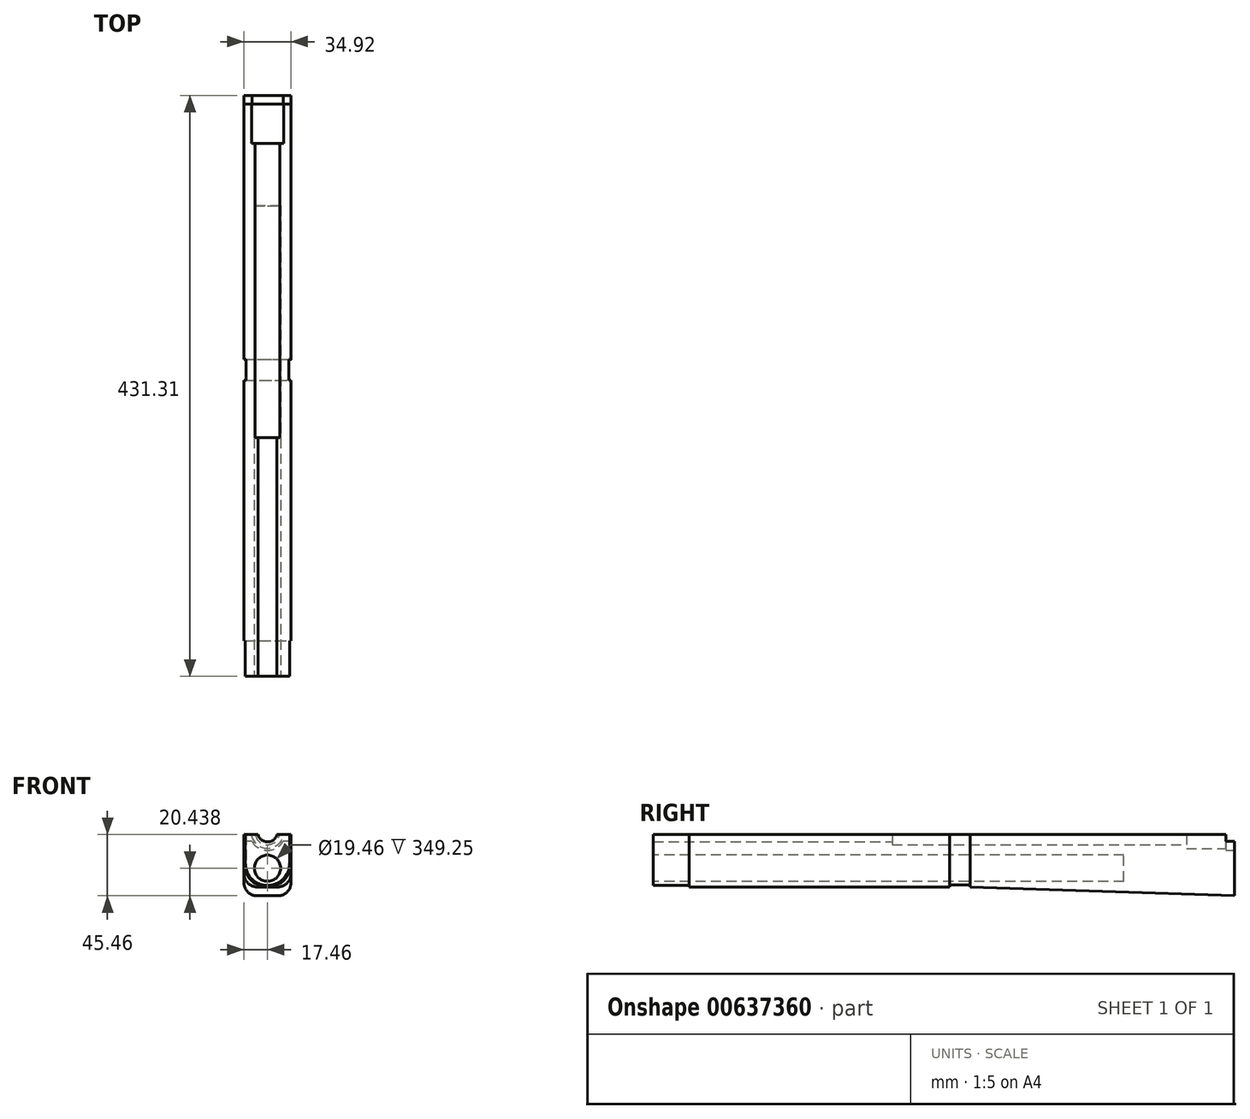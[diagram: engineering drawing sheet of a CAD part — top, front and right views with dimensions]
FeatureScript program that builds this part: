
annotation { "Feature Type Name" : "Feature", "Feature Type Description" : "" }
export const myFeature = defineFeature(function(context is Context, id is Id, definition is map)
    precondition{}
    {
        {
            var Q0;
            Q0=qCreatedBy(makeId("Front.planeOp"),FACE);
            var sketch = newSketch(context, id + "F0", { "sketchPlane" : qUnion([Q0])});
            skLineSegment(sketch, "E0", {"start": v(-17.45, -47.24) * mm, "end": v(17.45, -47.24) * mm});
            skLineSegment(sketch, "E1", {"start": v(-16.13, -1.78) * mm, "end": v(-16.13, -47.24) * mm});
            skLineSegment(sketch, "E2", {"start": v(16.13, -47.24) * mm, "end": v(16.13, -1.78) * mm});
            skLineSegment(sketch, "E3", {"start": v(-17.45, -1.78) * mm, "end": v(-17.45, -47.24) * mm});
            skLineSegment(sketch, "E4", {"start": v(17.45, -1.78) * mm, "end": v(12.57, -1.78) * mm});
            skLineSegment(sketch, "E5.trimOffspring", {"start": v(-12.57, -1.78) * mm, "end": v(-17.45, -1.78) * mm});
            skArc(sketch, "E6.converted", {"start": v(-12.57, -1.78) * mm, "mid": v(0, -12.7) * mm, "end": v(12.57, -1.78) * mm});
            skLineSegment(sketch, "E7", {"start": v(17.45, -6.83) * mm, "end": v(11.6, -6.83) * mm});
            skLineSegment(sketch, "E8", {"start": v(17.45, -1.78) * mm, "end": v(17.45, -47.24) * mm});
            skLineSegment(sketch, "E9.trimOffspring", {"start": v(-11.6, -6.83) * mm, "end": v(-17.45, -6.83) * mm});
            skArc(sketch, "E10.0", {"start": v(-13.34, -1.78) * mm, "mid": v(0, -13.46) * mm, "end": v(13.34, -1.78) * mm});
            skSolve(sketch);
        }
        {
            var Q0;
            {var subQ2=sQuery(id+"F0.wireOp",EDGE,"E2");Q0=makeQuery(id+"F0.imprint","IMPRINT",FACE,{"disambiguationData":[TD([[makeQuery(id+"F0.imprint","IMPRINT",EDGE,{"derivedFrom":subQ2}),-1.0]])]});}
            var Q1;
            {var subQ2=sQuery(id+"F0.wireOp",EDGE,"E1");Q1=makeQuery(id+"F0.imprint","IMPRINT",FACE,{"disambiguationData":[TD([[makeQuery(id+"F0.imprint","IMPRINT",EDGE,{"derivedFrom":subQ2}),-1.0]])]});}
            var Q2;
            {var subQ4=sQuery(id+"F0.wireOp",EDGE,"E1");Q2=makeQuery(id+"F0.imprint","IMPRINT",FACE,{"disambiguationData":[TD([[makeQuery(id+"F0.imprint","IMPRINT",EDGE,{"derivedFrom":subQ4}),1.0]])]});}
            var Q3;
            {var subQ0=sQuery(id+"F0.wireOp",EDGE,"E4");var subQ1=sQuery(id+"F0.wireOp",EDGE,"E2");var subQ2=makeQuery(id+"F0.imprint","INTERSECT",VERTEX,{"derivedFrom":[subQ1,subQ0]});Q3=makeQuery(id+"F0.imprint","IMPRINT",FACE,{"disambiguationData":[TD([[makeQuery(id+"F0.imprint","IMPRINT",EDGE,{"disambiguationData":[TD([[subQ2,1.0]])],"derivedFrom":subQ1}),1.0]])]});}
            var Q4;
            {var subQ0=sQuery(id+"F0.wireOp",EDGE,"E4");var subQ1=sQuery(id+"F0.wireOp",EDGE,"E2");var subQ2=makeQuery(id+"F0.imprint","INTERSECT",VERTEX,{"derivedFrom":[subQ1,subQ0]});Q4=makeQuery(id+"F0.imprint","IMPRINT",FACE,{"disambiguationData":[TD([[makeQuery(id+"F0.imprint","IMPRINT",EDGE,{"disambiguationData":[TD([[subQ2,1.0]])],"derivedFrom":subQ1}),-1.0]])]});}
            var Q5;
            {var subQ0=sQuery(id+"F0.wireOp",EDGE,"E5.trimOffspring");var subQ1=sQuery(id+"F0.wireOp",EDGE,"E1");var subQ2=makeQuery(id+"F0.imprint","INTERSECT",VERTEX,{"derivedFrom":[subQ1,subQ0]});Q5=makeQuery(id+"F0.imprint","IMPRINT",FACE,{"disambiguationData":[TD([[makeQuery(id+"F0.imprint","IMPRINT",EDGE,{"disambiguationData":[TD([[subQ2,-1.0]])],"derivedFrom":subQ1}),-1.0]])]});}
            var Q6;
            {var subQ5=sQuery(id+"F0.wireOp",EDGE,"E0");var subQ7=sQuery(id+"F0.wireOp",EDGE,"E1");var subQ8=makeQuery(id+"F0.imprint","INTERSECT",VERTEX,{"derivedFrom":[subQ5,subQ7]});Q6=makeQuery(id+"F0.imprint","IMPRINT",FACE,{"disambiguationData":[TD([[makeQuery(id+"F0.imprint","IMPRINT",EDGE,{"disambiguationData":[TD([[subQ8,-1.0]])],"derivedFrom":subQ5}),1.0]])]});}
            extrude(context, id + "F1", {"entities" : qUnion([Q0, Q1, Q2, Q3, Q4, Q5, Q6]), "depth" : 6.35 * mm, "offsetDistance" : 25.4 * mm});
        }
        {
            var Q0;
            Q0=makeQuery(id+"F1.opExtrude","CAP_FACE",FACE,{"disambiguationData":[OSD([sQuery(id+"F0.wireOp",EDGE,"E0"),sQuery(id+"F0.wireOp",EDGE,"8edb2757-4879-4a96-b7e5-693a79a6b6a4"),sQuery(id+"F0.wireOp",EDGE,"b94c221b-9bd1-4d43-af97-e907ac8222b8"),sQuery(id+"F0.wireOp",EDGE,"b538d115-4aab-44f9-98d3-6b26c575ee44"),sQuery(id+"F0.wireOp",EDGE,"78d40427-cc9b-45da-965b-9590cd821f86"),sQuery(id+"F0.wireOp",EDGE,"c01ce0f5-0f3a-4153-bfe7-1fc23657275d")])],"isStart":false});
            var sketch = newSketch(context, id + "F2", { "sketchPlane" : qUnion([Q0])});
            skLineSegment(sketch, "E11", {"start": v(-17.45, -47.24) * mm, "end": v(-17.45, -47.24) * mm});
            skArc(sketch, "E12", {"start": v(-11.93, -1.78) * mm, "mid": v(0, -12.07) * mm, "end": v(11.93, -1.78) * mm});
            skLineSegment(sketch, "E13", {"start": v(-16.13, -1.78) * mm, "end": v(-16.13, -47.24) * mm});
            skLineSegment(sketch, "E14", {"start": v(16.13, -1.78) * mm, "end": v(16.13, -47.24) * mm});
            skLineSegment(sketch, "E15", {"start": v(11.93, -1.78) * mm, "end": v(17.45, -1.78) * mm});
            skLineSegment(sketch, "E16", {"start": v(-11.93, -1.78) * mm, "end": v(-17.45, -1.78) * mm});
            skLineSegment(sketch, "E17", {"start": v(-17.45, -1.78) * mm, "end": v(-17.45, -47.24) * mm});
            skSolve(sketch);
        }
        {
            var Q0;
            {var subQ2=sQuery(id+"F2.wireOp",EDGE,"E13");Q0=makeQuery(id+"F2.imprint","IMPRINT",FACE,{"disambiguationData":[TD([[makeQuery(id+"F2.imprint","IMPRINT",EDGE,{"derivedFrom":subQ2}),1.0]])]});}
            var Q1;
            {var subQ0=sQuery(id+"F2.wireOp",EDGE,"E12");Q1=makeQuery(id+"F2.imprint","IMPRINT",FACE,{"disambiguationData":[TD([[makeQuery(id+"F2.imprint","IMPRINT",EDGE,{"derivedFrom":subQ0}),-1.0]])]});}
            var Q2;
            {var subQ0=sQuery(id+"F2.wireOp",EDGE,"E13");Q2=makeQuery(id+"F2.imprint","IMPRINT",FACE,{"disambiguationData":[TD([[makeQuery(id+"F2.imprint","IMPRINT",EDGE,{"derivedFrom":subQ0}),-1.0]])]});}
            var Q3;
            {var subQ0=sQuery(id+"F2.wireOp",EDGE,"E14");Q3=makeQuery(id+"F2.imprint","IMPRINT",FACE,{"disambiguationData":[TD([[makeQuery(id+"F2.imprint","IMPRINT",EDGE,{"derivedFrom":subQ0}),1.0]])]});}
            extrude(context, id + "F3", {"entities" : qUnion([Q0, Q1, Q2, Q3]), "operationType" : NewBodyOperationType.ADD, "depth" : 29.2 * mm, "offsetDistance" : 25.4 * mm});
        }
        {
            var Q0;
            Q0=makeQuery(id+"F3.opExtrude","CAP_FACE",FACE,{"disambiguationData":[OSD([sQuery(id+"F2.wireOp",EDGE,"E12"),sQuery(id+"F2.wireOp",EDGE,"E13"),sQuery(id+"F2.wireOp",EDGE,"E14"),sQuery(id+"F2.wireOp",EDGE,"f77e2a34-3a45-4c61-b7b2-087de49498f3"),sQuery(id+"F2.wireOp",EDGE,"be3fd59c-918e-4d32-9c2f-12a798890d1d"),sQuery(id+"F2.wireOp",EDGE,"E11")])],"isStart":false});
            var sketch = newSketch(context, id + "F4", { "sketchPlane" : qUnion([Q0])});
            skArc(sketch, "E18", {"start": v(-9.12, -1.78) * mm, "mid": v(0, -9.3) * mm, "end": v(9.12, -1.78) * mm});
            skLineSegment(sketch, "E19", {"start": v(-16.13, -1.78) * mm, "end": v(-16.13, -47.24) * mm});
            skLineSegment(sketch, "E20", {"start": v(16.13, -1.78) * mm, "end": v(16.13, -47.24) * mm});
            skLineSegment(sketch, "E21", {"start": v(17.45, -1.78) * mm, "end": v(9.12, -1.78) * mm});
            skLineSegment(sketch, "E22", {"start": v(-17.45, -1.78) * mm, "end": v(-9.12, -1.78) * mm});
            skLineSegment(sketch, "E23", {"start": v(-17.45, -47.24) * mm, "end": v(17.45, -47.24) * mm});
            skLineSegment(sketch, "E24", {"start": v(17.45, -47.24) * mm, "end": v(17.45, -1.78) * mm});
            skLineSegment(sketch, "E25", {"start": v(-17.45, -1.78) * mm, "end": v(-17.45, -47.24) * mm});
            skSolve(sketch);
        }
        {
            var Q0;
            Q0=qSketchRegion(id+"F4",true);
            extrude(context, id + "F5", {"entities" : qUnion([Q0]), "operationType" : NewBodyOperationType.ADD, "depth" : 160.5 * mm, "offsetDistance" : 25.4 * mm});
        }
        {
            var Q0;
            Q0=makeQuery(id+"F5.opExtrude","CAP_EDGE",EDGE,{"disambiguationData":[OSD([sQuery(id+"F4.wireOp",EDGE,"E23")])],"isStart":false});
            chamfer(context, id + "F6", {"entities" : qUnion([Q0]), "chamferType" : ChamferType.TWO_OFFSETS, "width1" : 6.6 * mm, "oppositeDirection" : false, "width2" : 196.06 * mm, "tangentPropagation" : true});
        }
        {
            var Q0;
            Q0=makeQuery(id+"F6.opChamfer","BLEND_EDGE",EDGE,{"blendedFrom":[makeQuery(id+"F5.opExtrude","CAP_EDGE",EDGE,{"disambiguationData":[OSD([sQuery(id+"F4.wireOp",EDGE,"E23")])],"isStart":false}),makeQuery(id+"F5.boolean.opBoolean","MERGE",FACE,{"derivedFrom":[makeQuery(id+"F3.boolean.opBoolean","MERGE",FACE,{"derivedFrom":[makeQuery(id+"F1.opExtrude","SWEPT_FACE",FACE,{"disambiguationData":[OSD([sQuery(id+"F0.wireOp",EDGE,"E3")])]}),makeQuery(id+"F3.opExtrude","SWEPT_FACE",FACE,{"disambiguationData":[OSD([sQuery(id+"F2.wireOp",EDGE,"E17")])]})]}),makeQuery(id+"F5.opExtrude","SWEPT_FACE",FACE,{"disambiguationData":[OSD([sQuery(id+"F4.wireOp",EDGE,"E25")])]})]})],"blendedInto":[makeQuery(id+"F5.boolean.opBoolean","MERGE",FACE,{"derivedFrom":[makeQuery(id+"F3.boolean.opBoolean","MERGE",FACE,{"derivedFrom":[makeQuery(id+"F1.opExtrude","SWEPT_FACE",FACE,{"disambiguationData":[OSD([sQuery(id+"F0.wireOp",EDGE,"E3")])]}),makeQuery(id+"F3.opExtrude","SWEPT_FACE",FACE,{"disambiguationData":[OSD([sQuery(id+"F2.wireOp",EDGE,"E17")])]})]}),makeQuery(id+"F5.opExtrude","SWEPT_FACE",FACE,{"disambiguationData":[OSD([sQuery(id+"F4.wireOp",EDGE,"E25")])]})]})]});
            var Q1;
            Q1=makeQuery(id+"F6.opChamfer","BLEND_EDGE",EDGE,{"blendedFrom":[makeQuery(id+"F5.opExtrude","CAP_EDGE",EDGE,{"disambiguationData":[OSD([sQuery(id+"F4.wireOp",EDGE,"E23")])],"isStart":false}),makeQuery(id+"F5.boolean.opBoolean","MERGE",FACE,{"derivedFrom":[makeQuery(id+"F3.boolean.opBoolean","MERGE",FACE,{"derivedFrom":[makeQuery(id+"F1.opExtrude","SWEPT_FACE",FACE,{"disambiguationData":[OSD([sQuery(id+"F0.wireOp",EDGE,"2a34f45b-83aa-449b-ac8a-cdb24f63008b")])]}),makeQuery(id+"F3.opExtrude","SWEPT_FACE",FACE,{"disambiguationData":[OSD([sQuery(id+"F2.wireOp",EDGE,"fa13c2eb-5be7-4b32-a947-3f863f632ee6")])]})]}),makeQuery(id+"F5.opExtrude","SWEPT_FACE",FACE,{"disambiguationData":[OSD([sQuery(id+"F4.wireOp",EDGE,"E24")])]})]})],"blendedInto":[makeQuery(id+"F5.boolean.opBoolean","MERGE",FACE,{"derivedFrom":[makeQuery(id+"F3.boolean.opBoolean","MERGE",FACE,{"derivedFrom":[makeQuery(id+"F1.opExtrude","SWEPT_FACE",FACE,{"disambiguationData":[OSD([sQuery(id+"F0.wireOp",EDGE,"2a34f45b-83aa-449b-ac8a-cdb24f63008b")])]}),makeQuery(id+"F3.opExtrude","SWEPT_FACE",FACE,{"disambiguationData":[OSD([sQuery(id+"F2.wireOp",EDGE,"fa13c2eb-5be7-4b32-a947-3f863f632ee6")])]})]}),makeQuery(id+"F5.opExtrude","SWEPT_FACE",FACE,{"disambiguationData":[OSD([sQuery(id+"F4.wireOp",EDGE,"E24")])]})]})]});
            fillet(context, id + "F7", {"entities" : qUnion([Q0, Q1]), "radius" : 9.65 * mm, "tangentPropagation" : true, "allowEdgeOverflow" : false});
        }
        {
            var Q0;
            Q0=makeQuery(id+"F5.opExtrude","CAP_FACE",FACE,{"disambiguationData":[OSD([sQuery(id+"F4.wireOp",EDGE,"E18"),sQuery(id+"F4.wireOp",EDGE,"E21"),sQuery(id+"F4.wireOp",EDGE,"E22"),sQuery(id+"F4.wireOp",EDGE,"E23"),sQuery(id+"F4.wireOp",EDGE,"E24"),sQuery(id+"F4.wireOp",EDGE,"E25")])],"isStart":false});
            var sketch = newSketch(context, id + "F8", { "sketchPlane" : qUnion([Q0])});
            skLineSegment(sketch, "E26.0", {"start": v(-15.92, -1.78) * mm, "end": v(-15.93, -23.19) * mm});
            skLineSegment(sketch, "E27.0", {"start": v(15.92, -1.78) * mm, "end": v(15.93, -23.19) * mm});
            skArc(sketch, "E28", {"start": v(-15.93, -23.19) * mm, "mid": v(0, -39.12) * mm, "end": v(15.93, -23.19) * mm});
            skLineSegment(sketch, "E29", {"start": v(-15.92, -1.78) * mm, "end": v(-9.12, -1.78) * mm});
            skLineSegment(sketch, "E30", {"start": v(15.92, -1.78) * mm, "end": v(9.12, -1.78) * mm});
            skArc(sketch, "E31", {"start": v(-9.12, -1.78) * mm, "mid": v(0, -9.3) * mm, "end": v(9.12, -1.78) * mm});
            skSolve(sketch);
        }
        {
            var Q0;
            Q0=makeQuery(id+"F8.imprint","IMPRINT",FACE,{"disambiguationData":[TD([[makeQuery(id+"F8.imprint","IMPRINT",EDGE,{"derivedFrom":sQuery(id+"F8.wireOp",EDGE,"E26.0")}),1.0]])]});
            extrude(context, id + "F9", {"entities" : qUnion([Q0]), "operationType" : NewBodyOperationType.ADD, "depth" : 15.42 * mm, "offsetDistance" : 25.4 * mm});
        }
        {
            var Q0;
            Q0=makeQuery(id+"F9.opExtrude","CAP_FACE",FACE,{"disambiguationData":[OSD([sQuery(id+"F8.wireOp",EDGE,"E26.0"),sQuery(id+"F8.wireOp",EDGE,"E27.0"),sQuery(id+"F8.wireOp",EDGE,"E28"),sQuery(id+"F8.wireOp",EDGE,"E29"),sQuery(id+"F8.wireOp",EDGE,"E30"),sQuery(id+"F8.wireOp",EDGE,"E31")])],"isStart":false});
            var sketch = newSketch(context, id + "F10", { "sketchPlane" : qUnion([Q0])});
            skLineSegment(sketch, "E32", {"start": v(9.12, -1.78) * mm, "end": v(17.46, -1.78) * mm});
            skArc(sketch, "E33", {"start": v(-9.12, -1.78) * mm, "mid": v(0, -9.3) * mm, "end": v(9.12, -1.78) * mm});
            skLineSegment(sketch, "E34.MirrorCS", {"start": v(-9.12, -1.78) * mm, "end": v(-17.46, -1.78) * mm});
            skLineSegment(sketch, "E35.MirrorCS", {"start": v(17.46, -1.78) * mm, "end": v(17.46, -23.18) * mm});
            skLineSegment(sketch, "E36.MirrorCS", {"start": v(-17.46, -1.78) * mm, "end": v(-17.46, -23.18) * mm});
            skArc(sketch, "E37", {"start": v(-17.46, -23.18) * mm, "mid": v(0, -40.64) * mm, "end": v(17.46, -23.18) * mm});
            skSolve(sketch);
        }
        {
            var Q0;
            {var subQ0=sQuery(id+"F10.wireOp",EDGE,"E35.MirrorCS");Q0=makeQuery(id+"F10.imprint","IMPRINT",FACE,{"disambiguationData":[TD([[makeQuery(id+"F10.imprint","IMPRINT",EDGE,{"derivedFrom":subQ0}),-1.0]])]});}
            var Q1;
            {var subQ2=sQuery(id+"F10.wireOp",EDGE,"E33");Q1=makeQuery(id+"F10.imprint","IMPRINT",FACE,{"disambiguationData":[TD([[makeQuery(id+"F10.imprint","IMPRINT",EDGE,{"derivedFrom":subQ2}),-1.0]])]});}
            extrude(context, id + "F11", {"entities" : qUnion([Q0, Q1]), "operationType" : NewBodyOperationType.ADD, "depth" : 42.52 * mm, "offsetDistance" : 25.4 * mm});
        }
        {
            var Q0;
            Q0=makeQuery(id+"F11.opExtrude","CAP_FACE",FACE,{"disambiguationData":[OSD([sQuery(id+"F10.wireOp",EDGE,"E32"),sQuery(id+"F10.wireOp",EDGE,"E33"),sQuery(id+"F10.wireOp",EDGE,"E34.MirrorCS"),sQuery(id+"F10.wireOp",EDGE,"E35.MirrorCS"),sQuery(id+"F10.wireOp",EDGE,"E36.MirrorCS"),sQuery(id+"F10.wireOp",EDGE,"E37")])],"isStart":false});
            var sketch = newSketch(context, id + "F12", { "sketchPlane" : qUnion([Q0])});
            skArc(sketch, "E38", {"start": v(-7.02, -1.78) * mm, "mid": v(0, -7.24) * mm, "end": v(7.02, -1.78) * mm});
            skLineSegment(sketch, "E39", {"start": v(17.46, -1.78) * mm, "end": v(7.02, -1.78) * mm});
            skLineSegment(sketch, "E40", {"start": v(-17.46, -1.78) * mm, "end": v(-17.46, -23.18) * mm});
            skLineSegment(sketch, "E41", {"start": v(17.46, -1.78) * mm, "end": v(17.46, -23.18) * mm});
            skArc(sketch, "E42", {"start": v(-17.46, -23.18) * mm, "mid": v(0, -40.64) * mm, "end": v(17.46, -23.18) * mm});
            skLineSegment(sketch, "E43", {"start": v(-17.46, -1.78) * mm, "end": v(-7.02, -1.78) * mm});
            skSolve(sketch);
        }
        {
            var Q0;
            {var subQ0=sQuery(id+"F12.wireOp",EDGE,"E38");Q0=makeQuery(id+"F12.imprint","IMPRINT",FACE,{"disambiguationData":[TD([[makeQuery(id+"F12.imprint","IMPRINT",EDGE,{"derivedFrom":subQ0}),-1.0]])]});}
            var Q1;
            {var subQ0=sQuery(id+"F12.wireOp",EDGE,"E40");Q1=makeQuery(id+"F12.imprint","IMPRINT",FACE,{"disambiguationData":[TD([[makeQuery(id+"F12.imprint","IMPRINT",EDGE,{"derivedFrom":subQ0}),1.0]])]});}
            extrude(context, id + "F13", {"entities" : qUnion([Q0, Q1]), "operationType" : NewBodyOperationType.ADD, "depth" : 177.32 * mm, "offsetDistance" : 25.4 * mm});
        }
        {
            var Q0;
            Q0=makeQuery(id+"F13.opExtrude","CAP_FACE",FACE,{"disambiguationData":[OSD([sQuery(id+"F12.wireOp",EDGE,"E38"),sQuery(id+"F12.wireOp",EDGE,"E39"),sQuery(id+"F12.wireOp",EDGE,"c7aa3f3b-c133-4458-a78d-b1247bf03585"),sQuery(id+"F12.wireOp",EDGE,"E40"),sQuery(id+"F12.wireOp",EDGE,"E41"),sQuery(id+"F12.wireOp",EDGE,"E42")])],"isStart":false});
            var sketch = newSketch(context, id + "F14", { "sketchPlane" : qUnion([Q0])});
            skLineSegment(sketch, "E44", {"start": v(17.46, -1.78) * mm, "end": v(16.44, -1.78) * mm});
            skLineSegment(sketch, "E45", {"start": v(-16.44, -1.78) * mm, "end": v(-17.46, -1.78) * mm});
            skLineSegment(sketch, "E46", {"start": v(-17.46, -1.78) * mm, "end": v(-17.46, -23.17) * mm});
            skLineSegment(sketch, "E47", {"start": v(17.46, -1.78) * mm, "end": v(17.46, -23.18) * mm});
            skArc(sketch, "E48", {"start": v(-17.46, -23.17) * mm, "mid": v(0, -40.64) * mm, "end": v(17.46, -23.17) * mm});
            skLineSegment(sketch, "E49.0", {"start": v(-16.44, -1.78) * mm, "end": v(-16.45, -23.18) * mm});
            skLineSegment(sketch, "E50.0", {"start": v(16.44, -1.78) * mm, "end": v(16.45, -23.18) * mm});
            skArc(sketch, "E51.0", {"start": v(-16.45, -23.18) * mm, "mid": v(0, -39.62) * mm, "end": v(16.45, -23.18) * mm});
            skCircle(sketch, "E52", {"center": v(0, -26.8) * mm, "radius": 9.73 * mm});
            skSolve(sketch);
        }
        {
            var Q0;
            Q0=makeQuery(id+"F14.imprint","IMPRINT",FACE,{"disambiguationData":[TD([[makeQuery(id+"F14.imprint","IMPRINT",EDGE,{"derivedFrom":sQuery(id+"F14.wireOp",EDGE,"E44")}),1.0]])]});
            extrude(context, id + "F15", {"entities" : qUnion([Q0]), "operationType" : NewBodyOperationType.REMOVE, "oppositeDirection" : true, "depth" : 26.5 * mm, "offsetDistance" : 25.4 * mm});
        }
        {
            var Q0;
            Q0=makeQuery(id+"F14.imprint","IMPRINT",FACE,{"disambiguationData":[TD([[makeQuery(id+"F14.imprint","IMPRINT",EDGE,{"derivedFrom":sQuery(id+"F14.wireOp",EDGE,"E52")}),1.0]])]});
            extrude(context, id + "F16", {"entities" : qUnion([Q0]), "operationType" : NewBodyOperationType.REMOVE, "oppositeDirection" : true, "depth" : 349.25 * mm, "offsetDistance" : 25.4 * mm});
        }
        {
            var Q0;
            {var subQ0=sQuery(id+"F0.wireOp",EDGE,"E4");var subQ1=sQuery(id+"F0.wireOp",EDGE,"E2");var subQ2=makeQuery(id+"F0.imprint","INTERSECT",VERTEX,{"derivedFrom":[subQ1,subQ0]});Q0=makeQuery(id+"F0.imprint","IMPRINT",FACE,{"disambiguationData":[TD([[makeQuery(id+"F0.imprint","IMPRINT",EDGE,{"disambiguationData":[TD([[subQ2,1.0]])],"derivedFrom":subQ1}),-1.0]])]});}
            var Q1;
            {var subQ0=sQuery(id+"F0.wireOp",EDGE,"E4");var subQ1=sQuery(id+"F0.wireOp",EDGE,"E2");var subQ2=makeQuery(id+"F0.imprint","INTERSECT",VERTEX,{"derivedFrom":[subQ1,subQ0]});Q1=makeQuery(id+"F0.imprint","IMPRINT",FACE,{"disambiguationData":[TD([[makeQuery(id+"F0.imprint","IMPRINT",EDGE,{"disambiguationData":[TD([[subQ2,1.0]])],"derivedFrom":subQ1}),1.0]])]});}
            var Q2;
            {var subQ0=sQuery(id+"F0.wireOp",EDGE,"E5.trimOffspring");var subQ1=sQuery(id+"F0.wireOp",EDGE,"E1");var subQ2=makeQuery(id+"F0.imprint","INTERSECT",VERTEX,{"derivedFrom":[subQ1,subQ0]});Q2=makeQuery(id+"F0.imprint","IMPRINT",FACE,{"disambiguationData":[TD([[makeQuery(id+"F0.imprint","IMPRINT",EDGE,{"disambiguationData":[TD([[subQ2,-1.0]])],"derivedFrom":subQ1}),1.0]])]});}
            var Q3;
            {var subQ0=sQuery(id+"F0.wireOp",EDGE,"E5.trimOffspring");var subQ1=sQuery(id+"F0.wireOp",EDGE,"E1");var subQ2=makeQuery(id+"F0.imprint","INTERSECT",VERTEX,{"derivedFrom":[subQ1,subQ0]});Q3=makeQuery(id+"F0.imprint","IMPRINT",FACE,{"disambiguationData":[TD([[makeQuery(id+"F0.imprint","IMPRINT",EDGE,{"disambiguationData":[TD([[subQ2,-1.0]])],"derivedFrom":subQ1}),-1.0]])]});}
            extrude(context, id + "F17", {"entities" : qUnion([Q0, Q1, Q2, Q3]), "operationType" : NewBodyOperationType.REMOVE, "depth" : 6.35 * mm, "offsetDistance" : 25.4 * mm});
        }
    });
